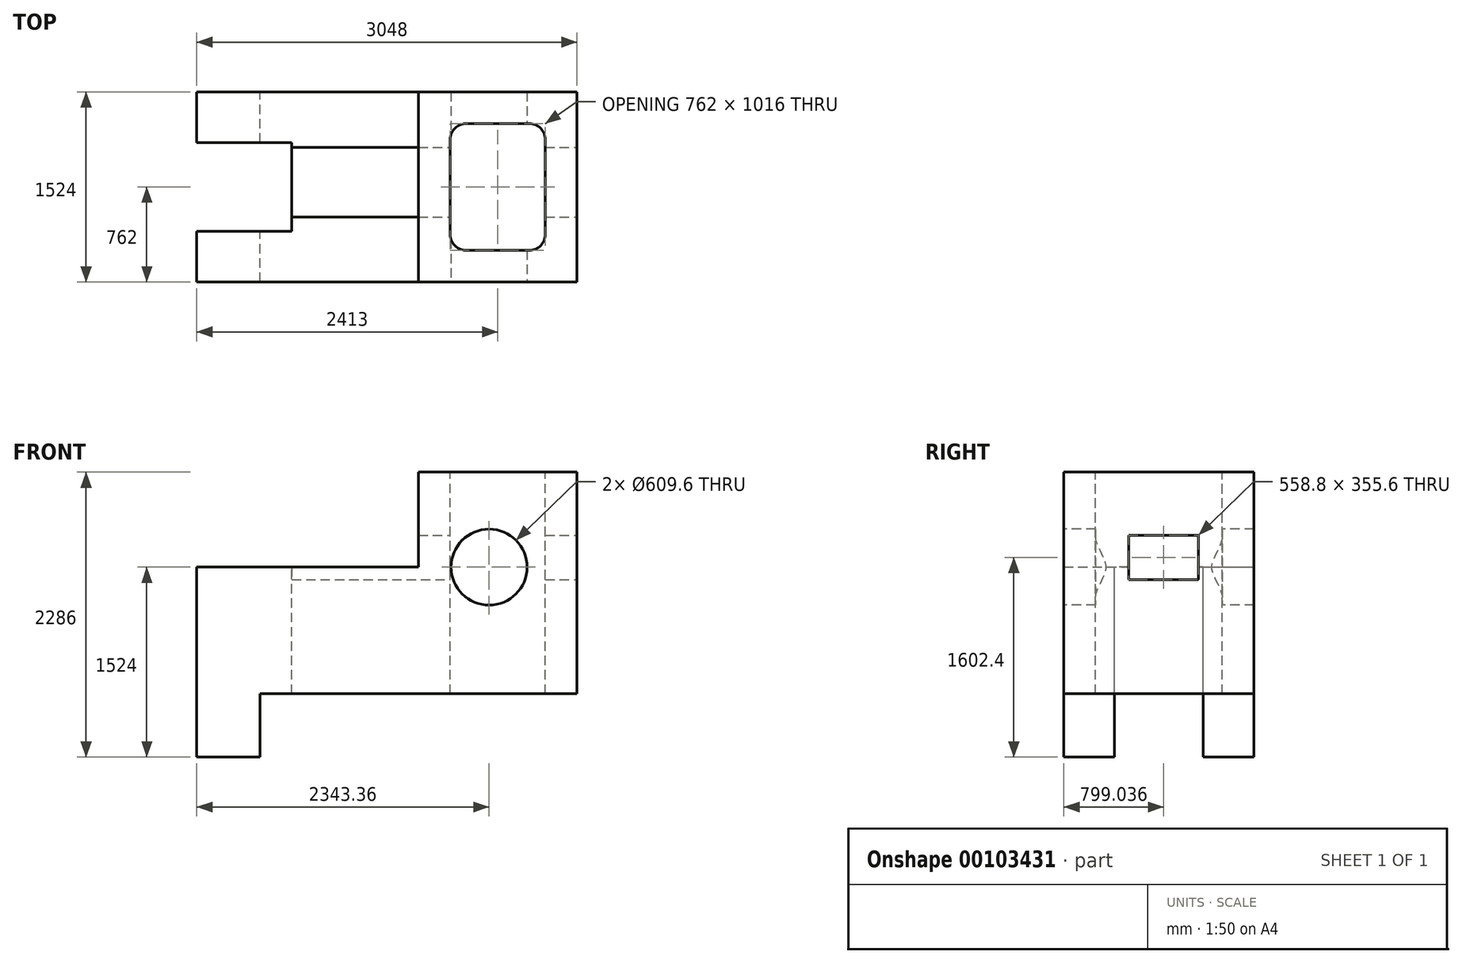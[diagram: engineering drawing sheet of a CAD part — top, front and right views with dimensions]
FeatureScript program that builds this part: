
annotation { "Feature Type Name" : "Feature", "Feature Type Description" : "" }
export const myFeature = defineFeature(function(context is Context, id is Id, definition is map)
    precondition{}
    {
        {
            var Q0;
            Q0=qCreatedBy(makeId("Front.planeOp"),FACE);
            var sketch = newSketch(context, id + "F0", { "sketchPlane" : qUnion([Q0])});
            skLineSegment(sketch, "E0", {"start": v(0, 0) * mm, "end": v(-1778, 0) * mm});
            skLineSegment(sketch, "E1", {"start": v(1270, -1016) * mm, "end": v(1270, 762) * mm});
            skLineSegment(sketch, "E2", {"start": v(1270, 762) * mm, "end": v(0, 762) * mm});
            skLineSegment(sketch, "E3", {"start": v(0, 762) * mm, "end": v(0, 0) * mm});
            skPoint(sketch, "E4.end.orphan", {"position": v(0, -482.31) * mm});
            skLineSegment(sketch, "E5", {"start": v(1270, -1016) * mm, "end": v(-1270, -1016) * mm});
            skLineSegment(sketch, "E6", {"start": v(-1778, -1016) * mm, "end": v(-1778, 0) * mm});
            skLineSegment(sketch, "E7", {"start": v(-1778, -1016) * mm, "end": v(-1778, -1524) * mm});
            skLineSegment(sketch, "E8", {"start": v(-1778, -1524) * mm, "end": v(-1270, -1524) * mm});
            skLineSegment(sketch, "E9", {"start": v(-1270, -1524) * mm, "end": v(-1270, -1016) * mm});
            skSolve(sketch);
        }
        {
            var Q0;
            Q0=makeQuery(id+"F0.imprint","IMPRINT",FACE,{"disambiguationData":[TD([[makeQuery(id+"F0.imprint","IMPRINT",EDGE,{"derivedFrom":sQuery(id+"F0.wireOp",EDGE,"E0")}),1.0]])]});
            extrude(context, id + "F1", {"entities" : qUnion([Q0]), "depth" : 1524 * mm});
        }
        {
            var Q0;
            Q0=makeQuery(id+"F1.opExtrude","SWEPT_FACE",FACE,{"disambiguationData":[OSD([sQuery(id+"F0.wireOp",EDGE,"E0")])]});
            var sketch = newSketch(context, id + "F2", { "sketchPlane" : qUnion([Q0])});
            skLineSegment(sketch, "E10.bottom", {"start": v(-1016, -406.4) * mm, "end": v(-1778, -406.4) * mm});
            skLineSegment(sketch, "E10.top", {"start": v(-1016, -1117.6) * mm, "end": v(-1778, -1117.6) * mm});
            skLineSegment(sketch, "E10.left", {"start": v(-1016, -406.4) * mm, "end": v(-1016, -1117.6) * mm});
            skPoint(sketch, "E10.middle", {"position": v(-1778, -762) * mm});
            skPoint(sketch, "E10.right.start.orphan", {"position": v(-2540, -406.4) * mm});
            skPoint(sketch, "E11.orphan", {"position": v(-2540, -1117.6) * mm});
            skSolve(sketch);
        }
        {
            var Q0;
            {var subQ0=sQuery(id+"F2.wireOp",EDGE,"E10.bottom");Q0=makeQuery(id+"F2.imprint","IMPRINT",FACE,{"disambiguationData":[TD([[makeQuery(id+"F2.imprint","IMPRINT",EDGE,{"derivedFrom":subQ0}),1.0]])]});}
            extrude(context, id + "F3", {"entities" : qUnion([Q0]), "operationType" : NewBodyOperationType.REMOVE, "oppositeDirection" : true, "depth" : 1524 * mm});
        }
        {
            var Q0;
            Q0=makeQuery(id+"F1.opExtrude","CAP_FACE",FACE,{"disambiguationData":[OSD([sQuery(id+"F0.wireOp",EDGE,"E0"),sQuery(id+"F0.wireOp",EDGE,"E1"),sQuery(id+"F0.wireOp",EDGE,"E2"),sQuery(id+"F0.wireOp",EDGE,"E3"),sQuery(id+"F0.wireOp",EDGE,"E5"),sQuery(id+"F0.wireOp",EDGE,"E6"),sQuery(id+"F0.wireOp",EDGE,"E7"),sQuery(id+"F0.wireOp",EDGE,"E8"),sQuery(id+"F0.wireOp",EDGE,"E9")])],"isStart":false});
            var sketch = newSketch(context, id + "F4", { "sketchPlane" : qUnion([Q0])});
            skCircle(sketch, "E12", {"center": v(565.36, 0) * mm, "radius": 304.8 * mm});
            skSolve(sketch);
        }
        {
            var Q0;
            Q0=makeQuery(id+"F4.imprint","IMPRINT",FACE,{"disambiguationData":[TD([[makeQuery(id+"F4.imprint","IMPRINT",EDGE,{"derivedFrom":sQuery(id+"F4.wireOp",EDGE,"E12")}),1.0]])]});
            extrude(context, id + "F5", {"entities" : qUnion([Q0]), "operationType" : NewBodyOperationType.REMOVE, "oppositeDirection" : true, "depth" : 1524 * mm});
        }
        {
            var Q0;
            Q0=makeQuery(id+"F1.opExtrude","SWEPT_FACE",FACE,{"disambiguationData":[OSD([sQuery(id+"F0.wireOp",EDGE,"E2")])]});
            var sketch = newSketch(context, id + "F6", { "sketchPlane" : qUnion([Q0])});
            skLineSegment(sketch, "E13.bottom", {"start": v(889, -1270) * mm, "end": v(381, -1270) * mm});
            skLineSegment(sketch, "E13.top", {"start": v(889, -254) * mm, "end": v(381, -254) * mm});
            skLineSegment(sketch, "E13.left", {"start": v(1016, -1143) * mm, "end": v(1016, -381) * mm});
            skLineSegment(sketch, "E13.right", {"start": v(254, -1143) * mm, "end": v(254, -381) * mm});
            skPoint(sketch, "E13.middle", {"position": v(635, -762) * mm});
            skPoint(sketch, "E13.middle.positionSnap0", {"position": v(635, -1524) * mm});
            skPoint(sketch, "E13.middle.positionSnap1", {"position": v(0, -762) * mm});
            skPoint(sketch, "E13.centerSnap0", {"position": v(635, -1524) * mm});
            skPoint(sketch, "E13.centerSnap1", {"position": v(0, -762) * mm});
            skPoint(sketch, "E14.visualSharp", {"position": v(254, -254) * mm});
            skArc(sketch, "E14.filletArc", {"start": v(381, -254) * mm, "mid": v(291.2, -291.2) * mm, "end": v(254, -381) * mm});
            skPoint(sketch, "E15.visualSharp", {"position": v(1016, -254) * mm});
            skArc(sketch, "E15.filletArc", {"start": v(1016, -381) * mm, "mid": v(978.8, -291.2) * mm, "end": v(889, -254) * mm});
            skPoint(sketch, "E16.visualSharp", {"position": v(1016, -1270) * mm});
            skArc(sketch, "E16.filletArc", {"start": v(889, -1270) * mm, "mid": v(978.8, -1232.8) * mm, "end": v(1016, -1143) * mm});
            skPoint(sketch, "E17.visualSharp", {"position": v(254, -1270) * mm});
            skArc(sketch, "E17.filletArc", {"start": v(254, -1143) * mm, "mid": v(291.2, -1232.8) * mm, "end": v(381, -1270) * mm});
            skSolve(sketch);
        }
        {
            var Q0;
            Q0=makeQuery(id+"F6.imprint","IMPRINT",FACE,{"disambiguationData":[TD([[makeQuery(id+"F6.imprint","IMPRINT",EDGE,{"derivedFrom":sQuery(id+"F6.wireOp",EDGE,"E13.bottom")}),-1.0]])]});
            extrude(context, id + "F7", {"entities" : qUnion([Q0]), "operationType" : NewBodyOperationType.REMOVE, "endBound" : BoundingType.THROUGH_ALL, "oppositeDirection" : true, "depth" : 1524 * mm});
        }
        {
            var Q0;
            Q0=makeQuery(id+"F1.opExtrude","SWEPT_FACE",FACE,{"disambiguationData":[OSD([sQuery(id+"F0.wireOp",EDGE,"E1")])]});
            var sketch = newSketch(context, id + "F8", { "sketchPlane" : qUnion([Q0])});
            skSolve(sketch);
        }
        {
            var Q0;
            {var subQ0=sQuery(id+"F0.wireOp",EDGE,"E1");Q0=makeQuery(id+"F8.imprint","IMPRINT",FACE,{"disambiguationData":[TD([[makeQuery(id+"F8.imprint","IMPRINT",EDGE,{"derivedFrom":makeQuery(id+"F1.opExtrude","CAP_EDGE",EDGE,{"disambiguationData":[OSD([subQ0])],"isStart":true})}),1.0]])]});}
            var sketch = newSketch(context, id + "F9", { "sketchPlane" : qUnion([Q0])});
            skLineSegment(sketch, "E18.bottom", {"start": v(-445.56, -99.4) * mm, "end": v(-1004.36, -99.4) * mm});
            skLineSegment(sketch, "E18.top", {"start": v(-445.56, 256.2) * mm, "end": v(-1004.36, 256.2) * mm});
            skLineSegment(sketch, "E18.left", {"start": v(-445.56, -99.4) * mm, "end": v(-445.56, 256.2) * mm});
            skLineSegment(sketch, "E18.right", {"start": v(-1004.36, -99.4) * mm, "end": v(-1004.36, 256.2) * mm});
            skPoint(sketch, "E18.middle", {"position": v(-724.96, 78.4) * mm});
            skSolve(sketch);
        }
        {
            var Q0;
            Q0=makeQuery(id+"F9.imprint","IMPRINT",FACE,{"disambiguationData":[TD([[makeQuery(id+"F9.imprint","IMPRINT",EDGE,{"derivedFrom":sQuery(id+"F9.wireOp",EDGE,"E18.bottom")}),-1.0]])]});
            extrude(context, id + "F10", {"entities" : qUnion([Q0]), "operationType" : NewBodyOperationType.REMOVE, "endBound" : BoundingType.THROUGH_ALL, "oppositeDirection" : true, "depth" : 1524 * mm});
        }
    });
